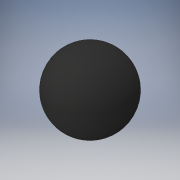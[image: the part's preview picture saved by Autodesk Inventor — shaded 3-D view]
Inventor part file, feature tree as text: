
AUTODESK INVENTOR PART (.ipt)
format: ipt  version: 2017 (Build 210142000, 142)  size: 122,880 bytes
history: native  units: in
note: dims shown in document units (in); Inventor stores cm internally (conversion verified against a paired STEP export)
features: fillet x2, extrude x1, sketch x1
ambient origin geometry x8: Origin, YZ Plane, XZ Plane, XY Plane, X Axis, Y Axis, Z Axis, Center Point
bodies: Solid1 (feature_tree)
feature tree (4):
  extrude  "Extrusion1"  Depth=10.5in TaperAngle=0.0deg
  fillet  "Fillet1"  Radius=10.5in
  sketch  "Sketch2"  dims[d0=21.0in d1=21.0in d2=0.0in d3=10.5in d4=10.5in d6=17.0in d7=10.5in d8=13.3698in]
  fillet  "Fillet2"  Radius=10.5in
